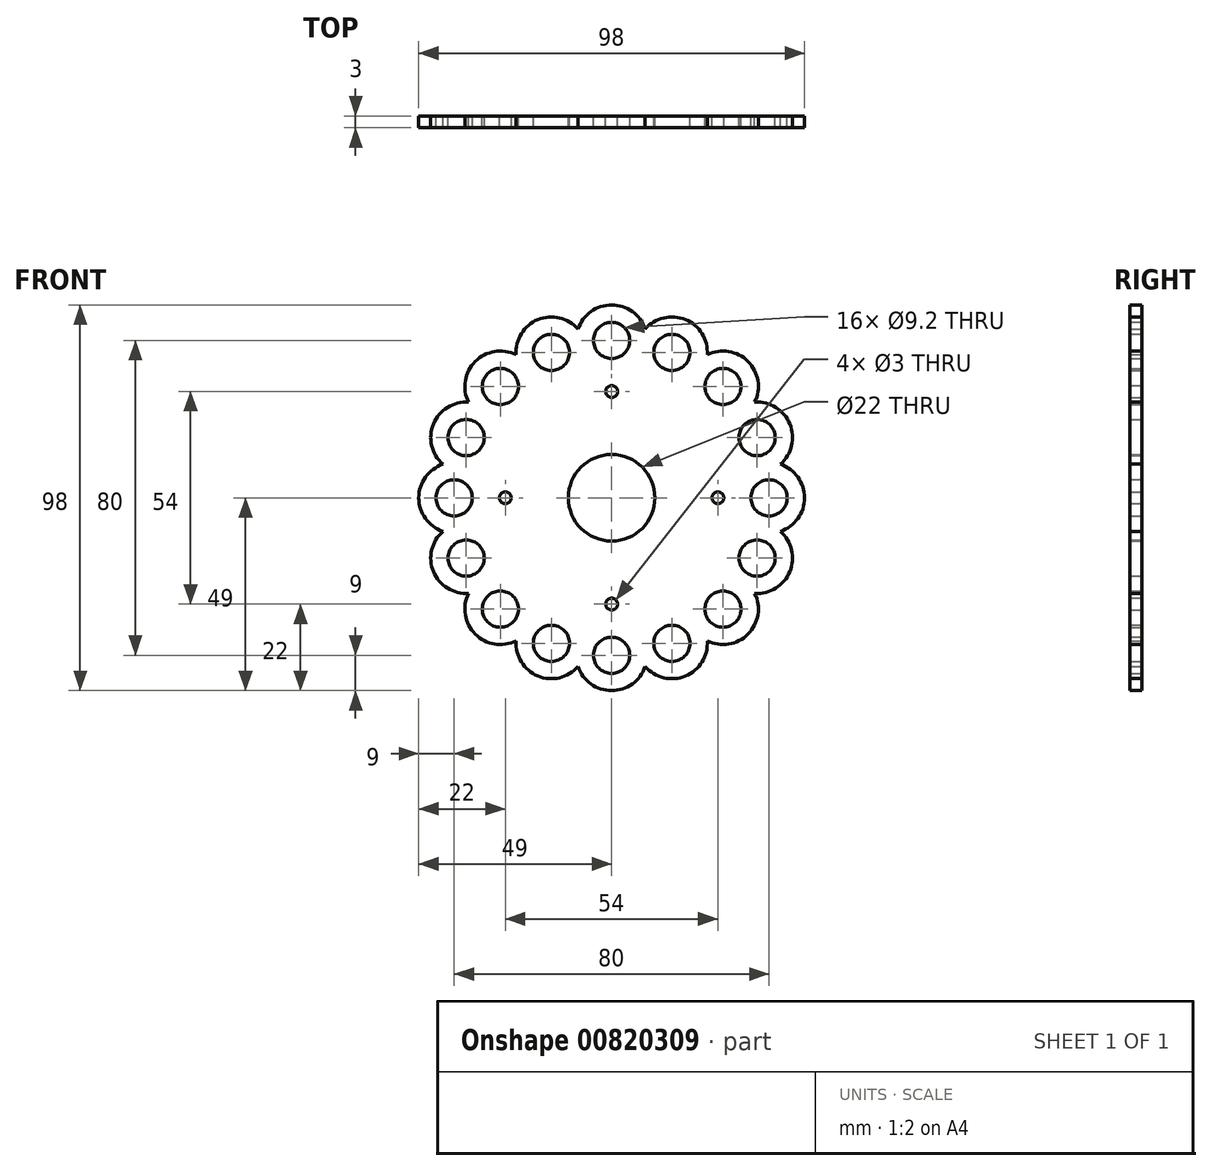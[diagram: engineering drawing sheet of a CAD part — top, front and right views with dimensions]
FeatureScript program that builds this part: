
annotation { "Feature Type Name" : "Feature", "Feature Type Description" : "" }
export const myFeature = defineFeature(function(context is Context, id is Id, definition is map)
    precondition{}
    {
        {
            var Q0;
            Q0=qCreatedBy(makeId("Front.planeOp"),FACE);
            var sketch = newSketch(context, id + "F0", { "sketchPlane" : qUnion([Q0])});
            skArc(sketch, "E0", {"start": v(2.15, 10.79) * mm, "mid": v(0, 11) * mm, "end": v(-2.15, 10.79) * mm});
            skCircle(sketch, "E1", {"center": v(0, 40) * mm, "radius": 4.6 * mm});
            skArc(sketch, "E2.trimOffspring", {"start": v(8.53, 42.88) * mm, "mid": v(0, 49) * mm, "end": v(-8.53, 42.88) * mm});
            skArc(sketch, "E3.1.0", {"start": v(-8.53, 42.88) * mm, "mid": v(-18.75, 45.27) * mm, "end": v(-24.29, 36.35) * mm});
            skCircle(sketch, "E3.1.1", {"center": v(-15.3, 36.96) * mm, "radius": 4.6 * mm});
            skArc(sketch, "E3.1.2", {"start": v(-2.15, 10.79) * mm, "mid": v(-4.2, 10.16) * mm, "end": v(-6.11, 9.15) * mm});
            skArc(sketch, "E3.2.0", {"start": v(-24.29, 36.35) * mm, "mid": v(-34.65, 34.65) * mm, "end": v(-36.35, 24.29) * mm});
            skCircle(sketch, "E3.2.1", {"center": v(-28.28, 28.28) * mm, "radius": 4.6 * mm});
            skArc(sketch, "E3.2.2", {"start": v(-6.11, 9.15) * mm, "mid": v(-7.78, 7.78) * mm, "end": v(-9.15, 6.11) * mm});
            skArc(sketch, "E3.3.0", {"start": v(-36.35, 24.29) * mm, "mid": v(-45.27, 18.75) * mm, "end": v(-42.88, 8.53) * mm});
            skCircle(sketch, "E3.3.1", {"center": v(-36.96, 15.3) * mm, "radius": 4.6 * mm});
            skArc(sketch, "E3.3.2", {"start": v(-9.15, 6.11) * mm, "mid": v(-10.16, 4.2) * mm, "end": v(-10.79, 2.15) * mm});
            skArc(sketch, "E3.4.0", {"start": v(-42.88, 8.53) * mm, "mid": v(-49, 0) * mm, "end": v(-42.88, -8.53) * mm});
            skCircle(sketch, "E3.4.1", {"center": v(-40, 0) * mm, "radius": 4.6 * mm});
            skArc(sketch, "E3.4.2", {"start": v(-10.79, 2.15) * mm, "mid": v(-11, 0) * mm, "end": v(-10.79, -2.15) * mm});
            skArc(sketch, "E3.5.0", {"start": v(-42.88, -8.53) * mm, "mid": v(-45.27, -18.75) * mm, "end": v(-36.35, -24.29) * mm});
            skCircle(sketch, "E3.5.1", {"center": v(-36.96, -15.3) * mm, "radius": 4.6 * mm});
            skArc(sketch, "E3.5.2", {"start": v(-10.79, -2.15) * mm, "mid": v(-10.16, -4.2) * mm, "end": v(-9.15, -6.11) * mm});
            skArc(sketch, "E3.6.0", {"start": v(-36.35, -24.29) * mm, "mid": v(-34.65, -34.65) * mm, "end": v(-24.29, -36.35) * mm});
            skCircle(sketch, "E3.6.1", {"center": v(-28.28, -28.28) * mm, "radius": 4.6 * mm});
            skArc(sketch, "E3.6.2", {"start": v(-9.15, -6.11) * mm, "mid": v(-7.78, -7.78) * mm, "end": v(-6.11, -9.15) * mm});
            skArc(sketch, "E3.7.0", {"start": v(-24.29, -36.35) * mm, "mid": v(-18.75, -45.27) * mm, "end": v(-8.53, -42.88) * mm});
            skCircle(sketch, "E3.7.1", {"center": v(-15.3, -36.96) * mm, "radius": 4.6 * mm});
            skArc(sketch, "E3.7.2", {"start": v(-6.11, -9.15) * mm, "mid": v(-4.2, -10.16) * mm, "end": v(-2.15, -10.79) * mm});
            skArc(sketch, "E3.8.0", {"start": v(-8.53, -42.88) * mm, "mid": v(0, -49) * mm, "end": v(8.53, -42.88) * mm});
            skCircle(sketch, "E3.8.1", {"center": v(0, -40) * mm, "radius": 4.6 * mm});
            skArc(sketch, "E3.8.2", {"start": v(-2.15, -10.79) * mm, "mid": v(0, -11) * mm, "end": v(2.15, -10.79) * mm});
            skArc(sketch, "E3.9.0", {"start": v(8.53, -42.88) * mm, "mid": v(18.75, -45.27) * mm, "end": v(24.29, -36.35) * mm});
            skCircle(sketch, "E3.9.1", {"center": v(15.3, -36.96) * mm, "radius": 4.6 * mm});
            skArc(sketch, "E3.9.2", {"start": v(2.15, -10.79) * mm, "mid": v(4.2, -10.16) * mm, "end": v(6.11, -9.15) * mm});
            skArc(sketch, "E3.10.0", {"start": v(24.29, -36.35) * mm, "mid": v(34.65, -34.65) * mm, "end": v(36.35, -24.29) * mm});
            skCircle(sketch, "E3.10.1", {"center": v(28.28, -28.28) * mm, "radius": 4.6 * mm});
            skArc(sketch, "E3.10.2", {"start": v(6.11, -9.15) * mm, "mid": v(7.78, -7.78) * mm, "end": v(9.15, -6.11) * mm});
            skArc(sketch, "E3.11.0", {"start": v(36.35, -24.29) * mm, "mid": v(45.27, -18.75) * mm, "end": v(42.88, -8.53) * mm});
            skCircle(sketch, "E3.11.1", {"center": v(36.96, -15.3) * mm, "radius": 4.6 * mm});
            skArc(sketch, "E3.11.2", {"start": v(9.15, -6.11) * mm, "mid": v(10.16, -4.2) * mm, "end": v(10.79, -2.15) * mm});
            skArc(sketch, "E3.12.0", {"start": v(42.88, -8.53) * mm, "mid": v(49, 0) * mm, "end": v(42.88, 8.53) * mm});
            skCircle(sketch, "E3.12.1", {"center": v(40, 0) * mm, "radius": 4.6 * mm});
            skArc(sketch, "E3.12.2", {"start": v(10.79, -2.15) * mm, "mid": v(11, 0) * mm, "end": v(10.79, 2.15) * mm});
            skArc(sketch, "E3.13.0", {"start": v(42.88, 8.53) * mm, "mid": v(45.27, 18.75) * mm, "end": v(36.35, 24.29) * mm});
            skCircle(sketch, "E3.13.1", {"center": v(36.96, 15.3) * mm, "radius": 4.6 * mm});
            skArc(sketch, "E3.13.2", {"start": v(10.79, 2.15) * mm, "mid": v(10.16, 4.2) * mm, "end": v(9.15, 6.11) * mm});
            skArc(sketch, "E3.14.0", {"start": v(36.35, 24.29) * mm, "mid": v(34.65, 34.65) * mm, "end": v(24.29, 36.35) * mm});
            skCircle(sketch, "E3.14.1", {"center": v(28.28, 28.28) * mm, "radius": 4.6 * mm});
            skArc(sketch, "E3.14.2", {"start": v(9.15, 6.11) * mm, "mid": v(7.78, 7.78) * mm, "end": v(6.11, 9.15) * mm});
            skArc(sketch, "E3.15.0", {"start": v(24.29, 36.35) * mm, "mid": v(18.75, 45.27) * mm, "end": v(8.53, 42.88) * mm});
            skCircle(sketch, "E3.15.1", {"center": v(15.3, 36.96) * mm, "radius": 4.6 * mm});
            skArc(sketch, "E3.15.2", {"start": v(6.11, 9.15) * mm, "mid": v(4.2, 10.16) * mm, "end": v(2.15, 10.79) * mm});
            skCircle(sketch, "E4", {"center": v(0, 27) * mm, "radius": 1.5 * mm});
            skCircle(sketch, "E5", {"center": v(27, 0) * mm, "radius": 1.5 * mm});
            skCircle(sketch, "E6", {"center": v(0, -27) * mm, "radius": 1.5 * mm});
            skCircle(sketch, "E7", {"center": v(-27, 0) * mm, "radius": 1.5 * mm});
            skSolve(sketch);
        }
        {
            var Q0;
            Q0=makeQuery(id+"F0.imprint","IMPRINT",FACE,{"disambiguationData":[TD([[makeQuery(id+"F0.imprint","IMPRINT",EDGE,{"derivedFrom":sQuery(id+"F0.wireOp",EDGE,"E0")}),-1.0]])]});
            extrude(context, id + "F1", {"entities" : qUnion([Q0]), "depth" : 3 * mm, "offsetDistance" : 25 * mm});
        }
    });
